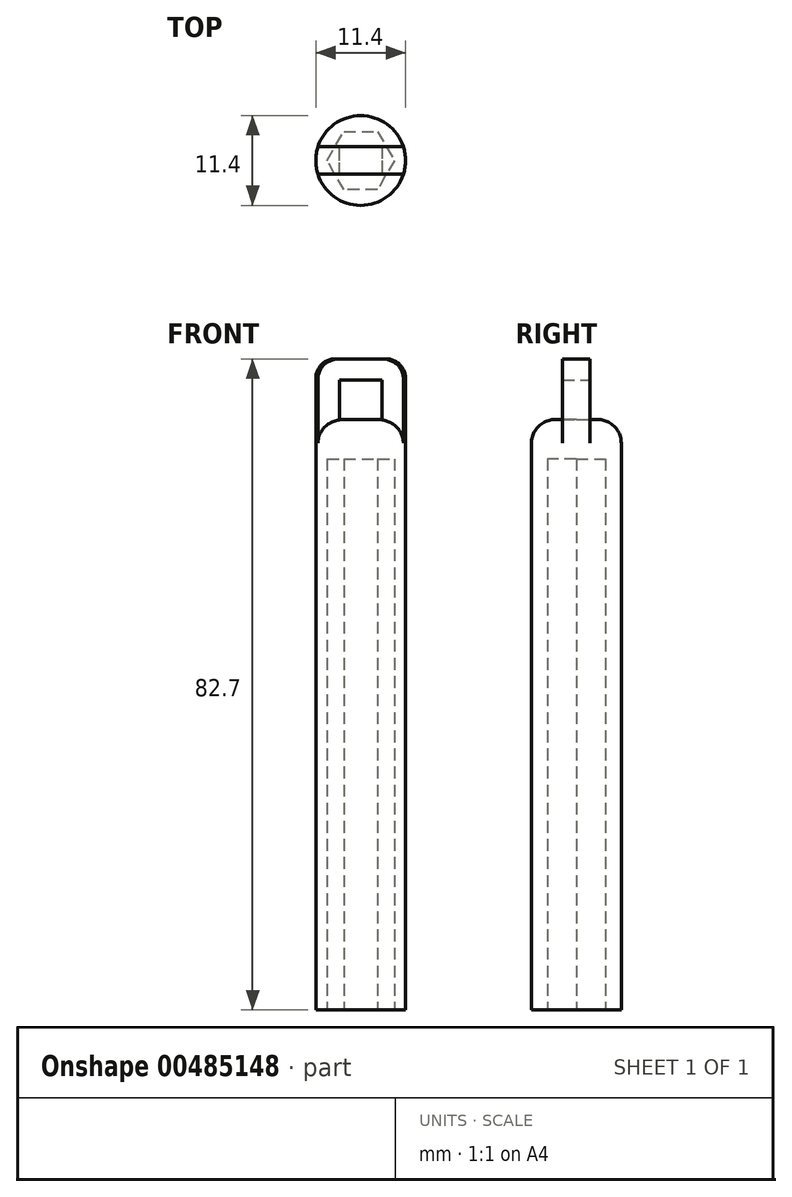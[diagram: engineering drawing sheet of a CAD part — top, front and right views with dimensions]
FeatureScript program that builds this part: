
annotation { "Feature Type Name" : "Feature", "Feature Type Description" : "" }
export const myFeature = defineFeature(function(context is Context, id is Id, definition is map)
    precondition{}
    {
        {
            var Q0;
            Q0=qCreatedBy(makeId("Top.planeOp"),FACE);
            var sketch = newSketch(context, id + "F0", { "sketchPlane" : qUnion([Q0])});
            skCircle(sketch, "E0.cCircle", {"center": v(0, 0) * mm, "radius": 3.4 * mm, "construction": true});
            skLineSegment(sketch, "E0.0", {"start": v(-1.96, 3.4) * mm, "end": v(1.96, 3.4) * mm});
            skLineSegment(sketch, "E0.1", {"start": v(1.96, 3.4) * mm, "end": v(3.93, 0) * mm});
            skLineSegment(sketch, "E0.2", {"start": v(3.93, 0) * mm, "end": v(1.96, -3.4) * mm});
            skLineSegment(sketch, "E0.3", {"start": v(1.96, -3.4) * mm, "end": v(-1.96, -3.4) * mm});
            skLineSegment(sketch, "E0.4", {"start": v(-1.96, -3.4) * mm, "end": v(-3.93, 0) * mm});
            skLineSegment(sketch, "E0.5", {"start": v(-3.93, 0) * mm, "end": v(-1.96, 3.4) * mm});
            skPoint(sketch, "E0.0.midPoint", {"position": v(0, 3.4) * mm});
            skLineSegment(sketch, "E1.0", {"start": v(-4.27, 0) * mm, "end": v(-2.14, 3.7) * mm});
            skLineSegment(sketch, "E1.1", {"start": v(2.14, 3.7) * mm, "end": v(4.27, 0) * mm});
            skLineSegment(sketch, "E1.2", {"start": v(4.27, 0) * mm, "end": v(2.14, -3.7) * mm});
            skLineSegment(sketch, "E1.3", {"start": v(-2.14, 3.7) * mm, "end": v(2.14, 3.7) * mm});
            skLineSegment(sketch, "E1.4", {"start": v(2.14, -3.7) * mm, "end": v(-2.14, -3.7) * mm});
            skLineSegment(sketch, "E1.5", {"start": v(-2.14, -3.7) * mm, "end": v(-4.27, 0) * mm});
            skLineSegment(sketch, "E2.0", {"start": v(-6.58, 0) * mm, "end": v(-3.3, 5.7) * mm, "construction": true});
            skLineSegment(sketch, "E2.1", {"start": v(3.3, 5.7) * mm, "end": v(6.58, 0) * mm, "construction": true});
            skLineSegment(sketch, "E2.2", {"start": v(6.58, 0) * mm, "end": v(3.3, -5.7) * mm, "construction": true});
            skLineSegment(sketch, "E2.3", {"start": v(-3.3, 5.7) * mm, "end": v(3.3, 5.7) * mm, "construction": true});
            skLineSegment(sketch, "E2.4", {"start": v(3.3, -5.7) * mm, "end": v(-3.3, -5.7) * mm, "construction": true});
            skLineSegment(sketch, "E2.5", {"start": v(-3.3, -5.7) * mm, "end": v(-6.58, 0) * mm, "construction": true});
            skCircle(sketch, "E3", {"center": v(0, 0) * mm, "radius": 5.7 * mm});
            skSolve(sketch);
        }
        {
            var Q0;
            Q0=makeQuery(id+"F0.imprint","IMPRINT",FACE,{"disambiguationData":[TD([[makeQuery(id+"F0.imprint","IMPRINT",EDGE,{"derivedFrom":sQuery(id+"F0.wireOp",EDGE,"E1.0")}),1.0]])]});
            extrude(context, id + "F1", {"entities" : qUnion([Q0]), "depth" : 70 * mm});
        }
        {
            var Q0;
            Q0=makeQuery(id+"F1.opExtrude","CAP_FACE",FACE,{"disambiguationData":[OSD([sQuery(id+"F0.wireOp",EDGE,"E1.0"),sQuery(id+"F0.wireOp",EDGE,"E1.1"),sQuery(id+"F0.wireOp",EDGE,"E1.2"),sQuery(id+"F0.wireOp",EDGE,"E1.3"),sQuery(id+"F0.wireOp",EDGE,"E1.4"),sQuery(id+"F0.wireOp",EDGE,"E1.5"),sQuery(id+"F0.wireOp",EDGE,"E3")])],"isStart":false});
            var sketch = newSketch(context, id + "F2", { "sketchPlane" : qUnion([Q0])});
            skSolve(sketch);
        }
        {
            var Q0;
            Q0=makeQuery(id+"F2.imprint","IMPRINT",FACE,{"disambiguationData":[TD([[makeQuery(id+"F2.imprint","IMPRINT",EDGE,{"derivedFrom":makeQuery(id+"F1.opExtrude","CAP_EDGE",EDGE,{"disambiguationData":[OSD([sQuery(id+"F0.wireOp",EDGE,"E1.0")])],"isStart":false})}),-1.0]])]});
            var Q1;
            Q1=makeQuery(id+"F2.imprint","IMPRINT",FACE,{"disambiguationData":[TD([[makeQuery(id+"F2.imprint","IMPRINT",EDGE,{"derivedFrom":makeQuery(id+"F1.opExtrude","CAP_EDGE",EDGE,{"disambiguationData":[OSD([sQuery(id+"F0.wireOp",EDGE,"E1.0")])],"isStart":false})}),1.0]])]});
            extrude(context, id + "F3", {"entities" : qUnion([Q0, Q1]), "operationType" : NewBodyOperationType.ADD, "depth" : 5 * mm});
        }
        {
            var Q0;
            Q0=makeQuery(id+"F3.opExtrude","CAP_FACE",FACE,{"disambiguationData":[OSD([sQuery(id+"F0.wireOp",EDGE,"E3")])],"isStart":false});
            var sketch = newSketch(context, id + "F4", { "sketchPlane" : qUnion([Q0])});
            skLineSegment(sketch, "E4.bottom", {"start": v(-2.7, -1.75) * mm, "end": v(-8.7, -1.75) * mm});
            skLineSegment(sketch, "E4.top", {"start": v(-2.7, 1.75) * mm, "end": v(-8.7, 1.75) * mm});
            skLineSegment(sketch, "E4.left", {"start": v(-2.7, -1.75) * mm, "end": v(-2.7, 1.75) * mm});
            skLineSegment(sketch, "E4.right", {"start": v(-8.7, -1.75) * mm, "end": v(-8.7, 1.75) * mm});
            skPoint(sketch, "E4.middle", {"position": v(-5.7, 0) * mm});
            skLineSegment(sketch, "E5.bottom", {"start": v(2.7, 1.75) * mm, "end": v(8.7, 1.75) * mm});
            skLineSegment(sketch, "E5.top", {"start": v(2.7, -1.75) * mm, "end": v(8.7, -1.75) * mm});
            skLineSegment(sketch, "E5.left", {"start": v(2.7, 1.75) * mm, "end": v(2.7, -1.75) * mm});
            skLineSegment(sketch, "E5.right", {"start": v(8.7, 1.75) * mm, "end": v(8.7, -1.75) * mm});
            skPoint(sketch, "E5.middle", {"position": v(5.7, 0) * mm});
            skSolve(sketch);
        }
        {
            var Q0;
            {var subQ0=sQuery(id+"F4.wireOp",EDGE,"E4.left");Q0=makeQuery(id+"F4.imprint","IMPRINT",FACE,{"disambiguationData":[TD([[makeQuery(id+"F4.imprint","IMPRINT",EDGE,{"derivedFrom":subQ0}),1.0]])]});}
            var Q1;
            {var subQ0=sQuery(id+"F4.wireOp",EDGE,"E5.left");Q1=makeQuery(id+"F4.imprint","IMPRINT",FACE,{"disambiguationData":[TD([[makeQuery(id+"F4.imprint","IMPRINT",EDGE,{"derivedFrom":subQ0}),1.0]])]});}
            extrude(context, id + "F5", {"entities" : qUnion([Q0, Q1]), "operationType" : NewBodyOperationType.ADD, "depth" : 5 * mm});
        }
        {
            var Q0;
            Q0=makeQuery(id+"F5.opExtrude","CAP_FACE",FACE,{"disambiguationData":[OSD([sQuery(id+"F0.wireOp",EDGE,"E3"),sQuery(id+"F4.wireOp",EDGE,"E4.bottom"),sQuery(id+"F4.wireOp",EDGE,"E4.top"),sQuery(id+"F4.wireOp",EDGE,"E4.left")])],"isStart":false});
            var sketch = newSketch(context, id + "F6", { "sketchPlane" : qUnion([Q0])});
            skLineSegment(sketch, "E6.0.0", {"start": v(2.7, 1.75) * mm, "end": v(2.7, -1.75) * mm});
            skLineSegment(sketch, "E6.0.1", {"start": v(2.7, -1.75) * mm, "end": v(5.42, -1.75) * mm});
            skArc(sketch, "E6.0.2", {"start": v(5.42, -1.75) * mm, "mid": v(5.7, 0) * mm, "end": v(5.42, 1.75) * mm});
            skLineSegment(sketch, "E6.0.3", {"start": v(5.42, 1.75) * mm, "end": v(2.7, 1.75) * mm});
            skLineSegment(sketch, "E7", {"start": v(2.7, 1.75) * mm, "end": v(-2.7, 1.75) * mm});
            skLineSegment(sketch, "E8", {"start": v(-2.7, -1.75) * mm, "end": v(2.7, -1.75) * mm});
            skSolve(sketch);
        }
        {
            var Q0;
            Q0=makeQuery(id+"F6.imprint","IMPRINT",FACE,{"disambiguationData":[TD([[makeQuery(id+"F6.imprint","IMPRINT",EDGE,{"derivedFrom":sQuery(id+"F6.wireOp",EDGE,"E6.0.0")}),-1.0]])]});
            var Q1;
            {var subQ0=sQuery(id+"F4.wireOp",EDGE,"E4.bottom");Q1=makeQuery(id+"F6.imprint","IMPRINT",FACE,{"disambiguationData":[TD([[makeQuery(id+"F6.imprint","IMPRINT",EDGE,{"derivedFrom":makeQuery(id+"F5.opExtrude","CAP_EDGE",EDGE,{"disambiguationData":[OSD([subQ0])],"isStart":false})}),-1.0]])]});}
            var Q2;
            Q2=makeQuery(id+"F6.imprint","IMPRINT",FACE,{"disambiguationData":[TD([[makeQuery(id+"F6.imprint","IMPRINT",EDGE,{"derivedFrom":sQuery(id+"F6.wireOp",EDGE,"E6.0.0")}),1.0]])]});
            extrude(context, id + "F7", {"entities" : qUnion([Q0, Q1, Q2]), "operationType" : NewBodyOperationType.ADD, "depth" : 2.7 * mm});
        }
        {
            var Q0;
            Q0=makeQuery(id+"F7.opExtrude","CAP_EDGE",EDGE,{"disambiguationData":[OSD([sQuery(id+"F0.wireOp",EDGE,"E3")])],"isStart":false});
            var Q1;
            Q1=makeQuery(id+"F5.opExtrude","CAP_EDGE",EDGE,{"disambiguationData":[OSD([sQuery(id+"F4.wireOp",EDGE,"E5.left")])],"isStart":false});
            var Q2;
            Q2=makeQuery(id+"F5.opExtrude","CAP_EDGE",EDGE,{"disambiguationData":[OSD([sQuery(id+"F4.wireOp",EDGE,"E4.left")])],"isStart":false});
            var Q3;
            Q3=makeQuery(id+"F7.opExtrude","CAP_EDGE",EDGE,{"disambiguationData":[OSD([sQuery(id+"F6.wireOp",EDGE,"E6.0.2")])],"isStart":false});
            fillet(context, id + "F8", {"entities" : qUnion([Q0, Q1, Q2, Q3]), "radius" : 2.5 * mm, "tangentPropagation" : true, "allowEdgeOverflow" : false});
        }
        {
            var Q0;
            Q0=makeQuery(id+"F3.opExtrude","CAP_EDGE",EDGE,{"disambiguationData":[OSD([sQuery(id+"F0.wireOp",EDGE,"E3")])],"isStart":false});
            fillet(context, id + "F9", {"entities" : qUnion([Q0]), "radius" : 3 * mm, "tangentPropagation" : true, "allowEdgeOverflow" : false});
        }
    });
